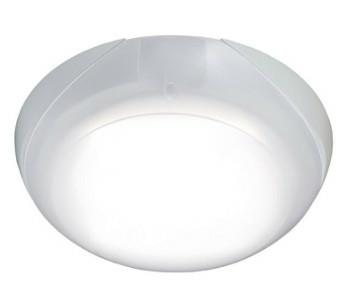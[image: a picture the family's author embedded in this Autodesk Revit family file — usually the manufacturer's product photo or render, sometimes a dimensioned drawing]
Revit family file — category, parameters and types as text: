
# Revit family: GALAD Кастор LED
name_source: partatom
category: Осветительные приборы
revit_build: Autodesk Revit 2018 (Build: 20180423_1000(x64)
units: mm (PartAtom-declared; Revit-internal decimal feet)

## family parameters
Источник света = Да
Общий = Нет
Основа = Грань
При загрузке вырезать с полостями = Нет
Размер круглого соединителя = Использовать диаметр
Тип детали = Нормальный
Точка расчета площади = Нет

## types (1)
- GALAD Кастор LED-25
    ADSK_Версия Revit = 2018
    ADSK_Версия семейства = 1.01
    ADSK_Единица измерения = шт.
    ADSK_Завод-изготовитель = Лихославльский завод 'Светотехника'
    ADSK_Классификация нагрузок = Освещение
    ADSK_Код изделия = 07123
    ADSK_Количество = 1
    ADSK_Количество фаз = 1
    ADSK_Коэффициент мощности = 0.95
    ADSK_Марка = GALAD Кастор LED-25
    ADSK_Масса = 1.2
    ADSK_Масса_Текст = 1.2
    ADSK_Наименование = GALAD Кастор LED-25
    ADSK_Наименование краткое = GALAD Кастор LED-25
    ADSK_Напряжение = 230 В
    ADSK_Номинальная мощность = 25 В·А
    ADSK_Обозначение = ГОСТ 15150-69, ГОСТ 12.2.007.0-
75, ГОСТ IEC 60598-2-3-2017
    ADSK_Полная мощность = 26 В·А
    ADSK_Размер_Высота = 94 мм
    ADSK_Размер_Длина = 310 мм
    ADSK_Размер_Ширина = 310 мм
    ADSK_Ток = 0 А
    ADSK_Энергоэффективность = 105 лм/Вт
    IP = 65
    URL = https://galad.ru
    Блок аварийного питания = Нет
    Видимая форма излучения при визуализации = Нет
    Возможный угол наклона = 0
    Группа модели = Светильники
    Диапазон цветовой температуры = 5028±283
    Изготовитель = Лихославльский завод 'Светотехника'
    Излучение по диаметру окружности = 610 мм
    Класс Защиты = 1
    Класс защиты от поражения электрическим током = 2
    Класс светораспределения = П
    Климатическая зона = У1
    Климатическое исполнение = -20…40 °С
    Коэффициент пульсации = менее 5%
    Материал корпуса = ПММА белый
    Материал рассеивателя = ПММА
    Неравномерность яркости = 0
    Область использования = ЖКХ
    Описание = Светодиодный светильник GALAD Кастор LED укомплектован матовым рассеивателем для минимизации слепящего действия и встроенным блоком питания. Ударопрочное защитное стекло выполнено из светостабилизированного поликарбоната. Установка светильника возможна на стену или на потолок.
    Отметка по умолчанию = 1219 мм
    Полная установленная мощность = 26 В·А
    Световая отдача = 105
    Светофильтр = 16777215
    Смещение цветовой температуры при затухании лампы = <Нет>
    Снижение светового потока во время разгорания = не более 6%
    Срок службы = 12 лет
    Тип КСС = Косинусная
    Тип ПРА = ЭПРА
    Тип источника света = LED
    Тип монтажной поверхности = настенный
    Тип продукции = Светильник
    Тип устройства управления светодиодами = без управления
    Угол наклона = -90.00°
    Файл фотометрической сетки = GALAD kastor LED-25.IES
    Цветопередача = 80
    Частота = 50
